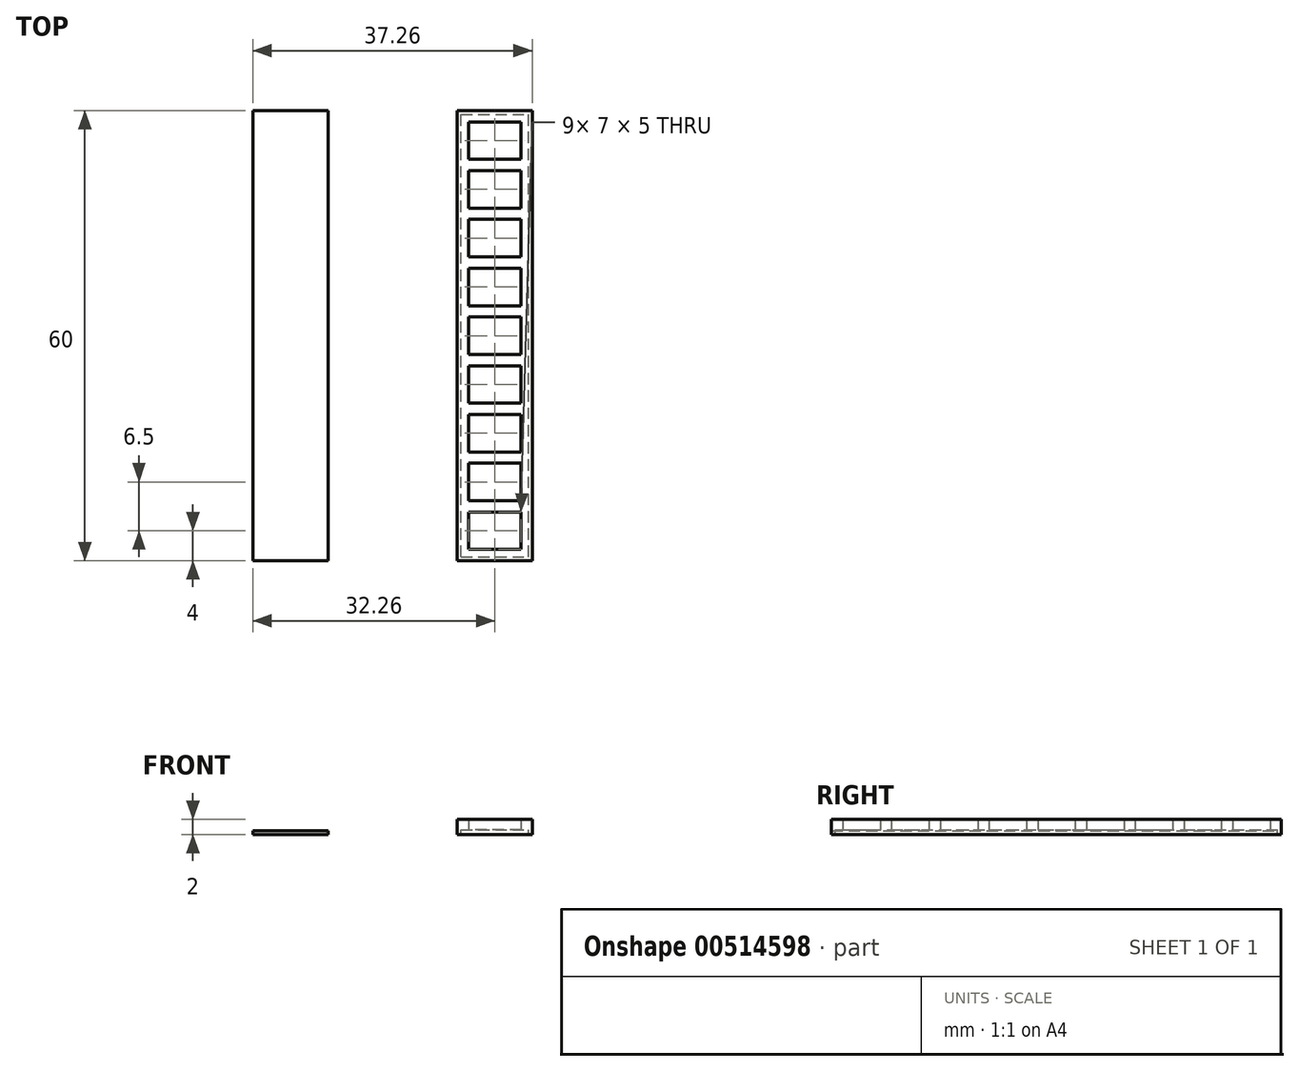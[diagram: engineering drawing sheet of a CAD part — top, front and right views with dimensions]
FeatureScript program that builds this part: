
annotation { "Feature Type Name" : "Feature", "Feature Type Description" : "" }
export const myFeature = defineFeature(function(context is Context, id is Id, definition is map)
    precondition{}
    {
        {
            var Q0;
            Q0=qCreatedBy(makeId("Top.planeOp"),FACE);
            var sketch = newSketch(context, id + "F0", { "sketchPlane" : qUnion([Q0])});
            skLineSegment(sketch, "E0.bottom", {"start": v(0, 0) * mm, "end": v(10, 0) * mm});
            skLineSegment(sketch, "E0.top", {"start": v(0, 60) * mm, "end": v(10, 60) * mm});
            skLineSegment(sketch, "E0.left", {"start": v(0, 0) * mm, "end": v(0, 60) * mm});
            skLineSegment(sketch, "E0.right", {"start": v(10, 0) * mm, "end": v(10, 60) * mm});
            skLineSegment(sketch, "E1.bottom", {"start": v(1.5, 58.5) * mm, "end": v(8.5, 58.5) * mm});
            skLineSegment(sketch, "E1.top", {"start": v(1.5, 1.5) * mm, "end": v(8.5, 1.5) * mm});
            skLineSegment(sketch, "E1.left", {"start": v(1.5, 58.5) * mm, "end": v(1.5, 53.5) * mm});
            skLineSegment(sketch, "E1.right", {"start": v(8.5, 58.5) * mm, "end": v(8.5, 53.5) * mm});
            skLineSegment(sketch, "E2", {"start": v(1.5, 53.5) * mm, "end": v(8.5, 53.5) * mm});
            skLineSegment(sketch, "E3", {"start": v(1.5, 52) * mm, "end": v(8.5, 52) * mm});
            skLineSegment(sketch, "E4.1.0.0", {"start": v(1.5, 45.5) * mm, "end": v(8.5, 45.5) * mm});
            skLineSegment(sketch, "E4.1.0.1", {"start": v(1.5, 47) * mm, "end": v(8.5, 47) * mm});
            skLineSegment(sketch, "E4.2.0.0", {"start": v(1.5, 39) * mm, "end": v(8.5, 39) * mm});
            skLineSegment(sketch, "E4.2.0.1", {"start": v(1.5, 40.5) * mm, "end": v(8.5, 40.5) * mm});
            skLineSegment(sketch, "E4.3.0.0", {"start": v(1.5, 32.5) * mm, "end": v(8.5, 32.5) * mm});
            skLineSegment(sketch, "E4.3.0.1", {"start": v(1.5, 34) * mm, "end": v(8.5, 34) * mm});
            skLineSegment(sketch, "E4.4.0.0", {"start": v(1.5, 26) * mm, "end": v(8.5, 26) * mm});
            skLineSegment(sketch, "E4.4.0.1", {"start": v(1.5, 27.5) * mm, "end": v(8.5, 27.5) * mm});
            skLineSegment(sketch, "E4.5.0.0", {"start": v(1.5, 19.5) * mm, "end": v(8.5, 19.5) * mm});
            skLineSegment(sketch, "E4.5.0.1", {"start": v(1.5, 21) * mm, "end": v(8.5, 21) * mm});
            skLineSegment(sketch, "E4.6.0.0", {"start": v(1.5, 13) * mm, "end": v(8.5, 13) * mm});
            skLineSegment(sketch, "E4.6.0.1", {"start": v(1.5, 14.5) * mm, "end": v(8.5, 14.5) * mm});
            skLineSegment(sketch, "E4.7.0.0", {"start": v(1.5, 6.5) * mm, "end": v(8.5, 6.5) * mm});
            skLineSegment(sketch, "E4.7.0.1", {"start": v(1.5, 8) * mm, "end": v(8.5, 8) * mm});
            skLineSegment(sketch, "E4.direction1", {"start": v(1.5, 52) * mm, "end": v(1.5, 47) * mm, "construction": true});
            skLineSegment(sketch, "E5.trimOffspring", {"start": v(8.5, 52) * mm, "end": v(8.5, 47) * mm});
            skLineSegment(sketch, "E6.trimOffspring", {"start": v(1.5, 52) * mm, "end": v(1.5, 47) * mm});
            skLineSegment(sketch, "E7.trimOffspring", {"start": v(8.5, 45.5) * mm, "end": v(8.5, 40.5) * mm});
            skLineSegment(sketch, "E8.trimOffspring", {"start": v(1.5, 45.5) * mm, "end": v(1.5, 40.5) * mm});
            skLineSegment(sketch, "E9.trimOffspring", {"start": v(8.5, 39) * mm, "end": v(8.5, 34) * mm});
            skLineSegment(sketch, "E10.trimOffspring", {"start": v(1.5, 39) * mm, "end": v(1.5, 34) * mm});
            skLineSegment(sketch, "E11.trimOffspring", {"start": v(8.5, 32.5) * mm, "end": v(8.5, 27.5) * mm});
            skLineSegment(sketch, "E12.trimOffspring", {"start": v(1.5, 32.5) * mm, "end": v(1.5, 27.5) * mm});
            skLineSegment(sketch, "E13.trimOffspring", {"start": v(8.5, 26) * mm, "end": v(8.5, 21) * mm});
            skLineSegment(sketch, "E14.trimOffspring", {"start": v(1.5, 26) * mm, "end": v(1.5, 21) * mm});
            skLineSegment(sketch, "E15.trimOffspring", {"start": v(8.5, 19.5) * mm, "end": v(8.5, 14.5) * mm});
            skLineSegment(sketch, "E16.trimOffspring", {"start": v(1.5, 19.5) * mm, "end": v(1.5, 14.5) * mm});
            skLineSegment(sketch, "E17.trimOffspring", {"start": v(8.5, 13) * mm, "end": v(8.5, 8) * mm});
            skLineSegment(sketch, "E18.trimOffspring", {"start": v(1.5, 13) * mm, "end": v(1.5, 8) * mm});
            skLineSegment(sketch, "E19.trimOffspring", {"start": v(8.5, 6.5) * mm, "end": v(8.5, 1.5) * mm});
            skLineSegment(sketch, "E20.trimOffspring", {"start": v(1.5, 6.5) * mm, "end": v(1.5, 1.5) * mm});
            skSolve(sketch);
        }
        {
            var Q0;
            Q0 = qSketchRegion(id + "F0", true);
            extrude(context, id + "F1", {"entities" : qUnion([Q0]), "depth" : 2 * mm, "offsetDistance" : 25 * mm});
        }
        {
            var Q0;
            Q0=qCreatedBy(makeId("Top.planeOp"),FACE);
            var sketch = newSketch(context, id + "F2", { "sketchPlane" : qUnion([Q0])});
            skLineSegment(sketch, "E21.bottom", {"start": v(-17.26, 0) * mm, "end": v(-27.26, 0) * mm});
            skLineSegment(sketch, "E21.top", {"start": v(-17.26, 60) * mm, "end": v(-27.26, 60) * mm});
            skLineSegment(sketch, "E21.left", {"start": v(-17.26, 0) * mm, "end": v(-17.26, 60) * mm});
            skLineSegment(sketch, "E21.right", {"start": v(-27.26, 0) * mm, "end": v(-27.26, 60) * mm});
            skSolve(sketch);
        }
        {
            var Q0;
            Q0 = qSketchRegion(id + "F2", true);
            extrude(context, id + "F3", {"entities" : qUnion([Q0]), "depth" : 0.5 * mm, "offsetDistance" : 25 * mm});
        }
        {
            var Q0;
            Q0=makeQuery(id+"F1.opExtrude","CAP_FACE",FACE,{"disambiguationData":[OSD([sQuery(id+"F0.wireOp",EDGE,"E0.bottom"),sQuery(id+"F0.wireOp",EDGE,"E0.top"),sQuery(id+"F0.wireOp",EDGE,"E0.left"),sQuery(id+"F0.wireOp",EDGE,"E0.right"),sQuery(id+"F0.wireOp",EDGE,"E1.bottom"),sQuery(id+"F0.wireOp",EDGE,"E1.top"),sQuery(id+"F0.wireOp",EDGE,"E1.left"),sQuery(id+"F0.wireOp",EDGE,"E1.right"),sQuery(id+"F0.wireOp",EDGE,"E2"),sQuery(id+"F0.wireOp",EDGE,"E3"),sQuery(id+"F0.wireOp",EDGE,"E4.1.0.0"),sQuery(id+"F0.wireOp",EDGE,"E4.1.0.1"),sQuery(id+"F0.wireOp",EDGE,"E4.2.0.0"),sQuery(id+"F0.wireOp",EDGE,"E4.2.0.1"),sQuery(id+"F0.wireOp",EDGE,"E4.3.0.0"),sQuery(id+"F0.wireOp",EDGE,"E4.3.0.1"),sQuery(id+"F0.wireOp",EDGE,"E4.4.0.0"),sQuery(id+"F0.wireOp",EDGE,"E4.4.0.1"),sQuery(id+"F0.wireOp",EDGE,"E4.5.0.0"),sQuery(id+"F0.wireOp",EDGE,"E4.5.0.1"),sQuery(id+"F0.wireOp",EDGE,"E4.6.0.0"),sQuery(id+"F0.wireOp",EDGE,"E4.6.0.1"),sQuery(id+"F0.wireOp",EDGE,"E4.7.0.0"),sQuery(id+"F0.wireOp",EDGE,"E4.7.0.1"),sQuery(id+"F0.wireOp",EDGE,"E5.trimOffspring"),sQuery(id+"F0.wireOp",EDGE,"E6.trimOffspring"),sQuery(id+"F0.wireOp",EDGE,"E7.trimOffspring"),sQuery(id+"F0.wireOp",EDGE,"E8.trimOffspring"),sQuery(id+"F0.wireOp",EDGE,"E9.trimOffspring"),sQuery(id+"F0.wireOp",EDGE,"E10.trimOffspring"),sQuery(id+"F0.wireOp",EDGE,"E11.trimOffspring"),sQuery(id+"F0.wireOp",EDGE,"E12.trimOffspring"),sQuery(id+"F0.wireOp",EDGE,"E13.trimOffspring"),sQuery(id+"F0.wireOp",EDGE,"E14.trimOffspring"),sQuery(id+"F0.wireOp",EDGE,"E15.trimOffspring"),sQuery(id+"F0.wireOp",EDGE,"E16.trimOffspring"),sQuery(id+"F0.wireOp",EDGE,"E17.trimOffspring"),sQuery(id+"F0.wireOp",EDGE,"E18.trimOffspring"),sQuery(id+"F0.wireOp",EDGE,"E19.trimOffspring"),sQuery(id+"F0.wireOp",EDGE,"E20.trimOffspring")])],"isStart":true});
            var sketch = newSketch(context, id + "F4", { "sketchPlane" : qUnion([Q0])});
            skLineSegment(sketch, "E22", {"start": v(0, 0) * mm, "end": v(0.5, 0) * mm, "construction": true});
            skLineSegment(sketch, "E23", {"start": v(0.5, 0) * mm, "end": v(0.5, -0.5) * mm, "construction": true});
            skLineSegment(sketch, "E24.bottom", {"start": v(0.5, -0.5) * mm, "end": v(9.5, -0.5) * mm});
            skLineSegment(sketch, "E24.top", {"start": v(0.5, -59.5) * mm, "end": v(9.5, -59.5) * mm});
            skLineSegment(sketch, "E24.left", {"start": v(0.5, -0.5) * mm, "end": v(0.5, -59.5) * mm});
            skLineSegment(sketch, "E24.right", {"start": v(9.5, -0.5) * mm, "end": v(9.5, -59.5) * mm});
            skSolve(sketch);
        }
        {
            var Q0;
            Q0 = qSketchRegion(id + "F4", true);
            extrude(context, id + "F5", {"entities" : qUnion([Q0]), "operationType" : NewBodyOperationType.REMOVE, "oppositeDirection" : true, "depth" : 0.6 * mm, "offsetDistance" : 25 * mm});
        }
        {
            var Q0;
            Q0=makeQuery(id+"F5.boolean.opBoolean","COPY",FACE,{"derivedFrom":makeQuery(id+"F5.opExtrude","CAP_FACE",FACE,{"disambiguationData":[OSD([sQuery(id+"F4.wireOp",EDGE,"E24.bottom"),sQuery(id+"F4.wireOp",EDGE,"E24.top"),sQuery(id+"F4.wireOp",EDGE,"E24.left"),sQuery(id+"F4.wireOp",EDGE,"E24.right")])],"isStart":false})});
            var sketch = newSketch(context, id + "F6", { "sketchPlane" : qUnion([Q0])});
            skLineSegment(sketch, "E25.bottom", {"start": v(0.5, -0.5) * mm, "end": v(9.5, -0.5) * mm});
            skLineSegment(sketch, "E25.top", {"start": v(0.5, -59.5) * mm, "end": v(9.5, -59.5) * mm});
            skLineSegment(sketch, "E25.left", {"start": v(0.5, -0.5) * mm, "end": v(0.5, -59.5) * mm});
            skLineSegment(sketch, "E25.right", {"start": v(9.5, -0.5) * mm, "end": v(9.5, -59.5) * mm});
            skSolve(sketch);
        }
        {
            var Q0;
            Q0 = qSketchRegion(id + "F6", true);
            extrude(context, id + "F7", {"entities" : qUnion([Q0]), "depth" : 0.6 * mm, "offsetDistance" : 25 * mm});
        }
    });
